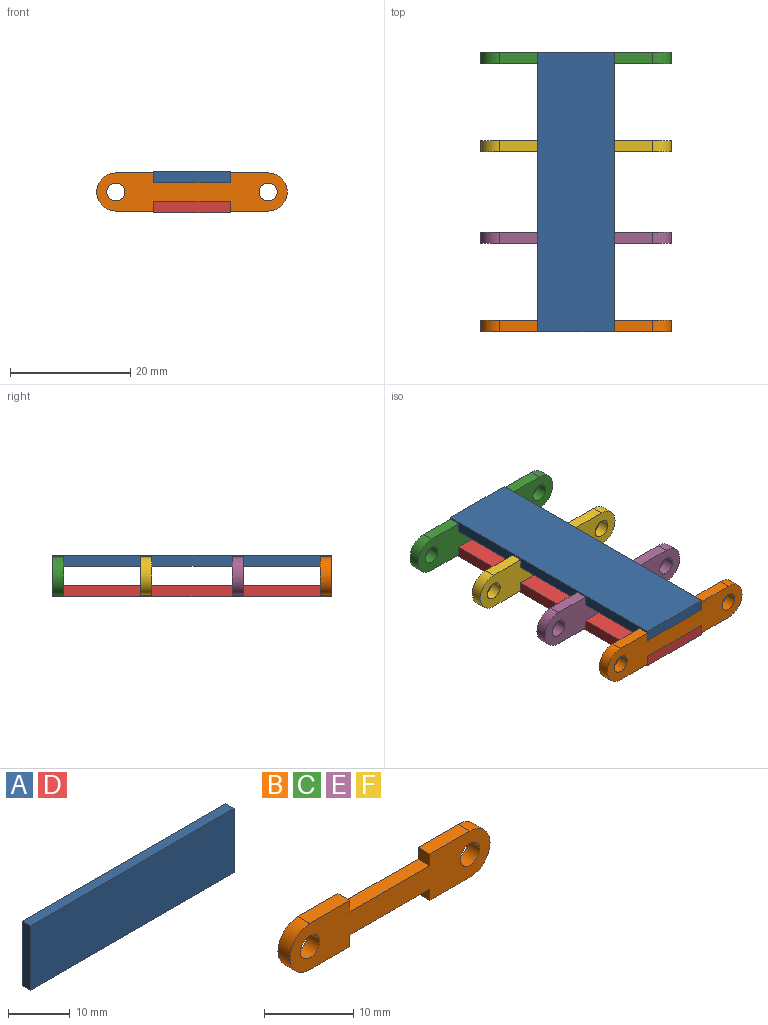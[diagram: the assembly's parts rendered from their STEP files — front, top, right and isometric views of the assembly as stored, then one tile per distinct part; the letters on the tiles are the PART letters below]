
ASSEMBLY  parts=6 mates=5
PART A: 6 faces, bbox 46.5x1.9x12.7 mm
  f0: plane 46.48x1.9mm, normal (0,0,-1), area 88.2mm2, adj f1,f3,f4,f5
  f1: plane 12.7x1.9mm, normal (1,0,0), area 24.1mm2, adj f0,f2,f4,f5
  f2: plane 46.48x1.9mm, normal (0,0,1), area 88.2mm2, adj f1,f3,f4,f5
  f3: plane 12.7x1.9mm, normal (-1,0,0), area 24.1mm2, adj f0,f2,f4,f5
  f4: plane 46.48x12.7mm, normal (0,-1,0), area 590.3mm2, adj f0,f1,f2,f3
  f5: plane 46.48x12.7mm, normal (0,1,0), area 590.3mm2, adj f0,f1,f2,f3
PART B: 20 faces, bbox 31.7x1.9x6.4 mm
  f0: plane 6.35x1.9mm, normal (0,0,-1), area 12mm2, adj f1,f15,f18,f19
  f1: plane 1.9x1.59mm, normal (1,0,0), area 3mm2, adj f0,f2,f18,f19
  f2: plane 12.7x1.9mm, normal (0,0,-1), area 24.1mm2, adj f1,f3,f18,f19
  f3: plane 1.9x1.59mm, normal (-1,0,0), area 3mm2, adj f2,f4,f18,f19
  f4: plane 6.35x1.9mm, normal (0,0,-1), area 12mm2, adj f3,f5,f18,f19
  f5: plane 1.9x0mm, normal (1,0,0), area 0mm2, adj f4,f6,f18,f19
  f6: cylinder r=3.17mm len=6.35mm, axis (0,1,0), area 18.9mm2, adj f5,f7,f18,f19
  f7: plane 1.9x0mm, normal (1,0,0), area 0mm2, adj f6,f8,f18,f19
  f8: plane 6.35x1.9mm, normal (0,0,1), area 12mm2, adj f7,f9,f18,f19
  f9: plane 1.9x1.59mm, normal (-1,0,0), area 3mm2, adj f8,f10,f18,f19
  f10: plane 12.7x1.9mm, normal (0,0,1), area 24.1mm2, adj f9,f11,f18,f19
  f11: plane 1.9x1.59mm, normal (1,0,0), area 3mm2, adj f10,f12,f18,f19
  f12: plane 6.35x1.9mm, normal (0,0,1), area 12mm2, adj f11,f13,f18,f19
  f13: plane 1.9x0.01mm, normal (-1,0,0), area 0mm2, adj f12,f14,f18,f19
  f14: cylinder r=3.17mm len=6.34mm, axis (0,1,0), area 18.9mm2, adj f13,f15,f18,f19
  f15: plane 1.9x0.01mm, normal (-1,0,0), area 0mm2, adj f0,f14,f18,f19
  f16: cylinder r=1.5mm len=3mm, axis (0,1,0), area 17.9mm2, adj f18,f19
  f17: cylinder r=1.5mm len=3mm, axis (0,1,0), area 17.9mm2, adj f18,f19
  f18: plane 31.74x6.35mm, normal (0,-1,0), area 138.4mm2, adj f0,f1,f2,f3,f4,f5,f6,f7
  f19: plane 31.74x6.35mm, normal (0,1,0), area 138.4mm2, adj f0,f1,f2,f3,f4,f5,f6,f7
PART C: same geometry as B
PART D: same geometry as A
PART E: same geometry as B
PART F: same geometry as B
PLACE A rot(axis=(-0.58,-0.58,0.58),120deg) t=(-85.54,30.05,-15.68)mm
PLACE B rot(axis=(-0.66,0.54,0.53),0deg) t=(-31.14,-30.47,-58.33)mm
PLACE C rot(axis=(-0.66,0.54,0.53),0deg) t=(-31.14,14.12,-58.33)mm
PLACE D rot(axis=(-0.58,-0.58,0.58),120deg) t=(-85.54,30.05,-20.76)mm
PLACE E rot(axis=(-0.66,0.54,0.53),0deg) t=(-31.14,-15.79,-58.33)mm
PLACE F t=(-31.14,-0.55,-58.33)mm
MATE fastened E.f2 <-> D.f4  axis (0,0,-1) through (-79.19,-16.74,-18.86)mm
MATE fastened A.f5 <-> B.f10  axis (0,0,-1) through (-79.19,-32.36,-15.68)mm
MATE fastened F.f2 <-> D.f4  axis (0,0,-1) through (-79.19,-1.5,-18.86)mm
MATE fastened B.f18 <-> D.f3  axis (0,-1,0) through (-79.19,-32.36,-18.86)mm
MATE fastened C.f19 <-> D.f1  axis (0,1,0) through (-79.19,14.12,-18.86)mm
